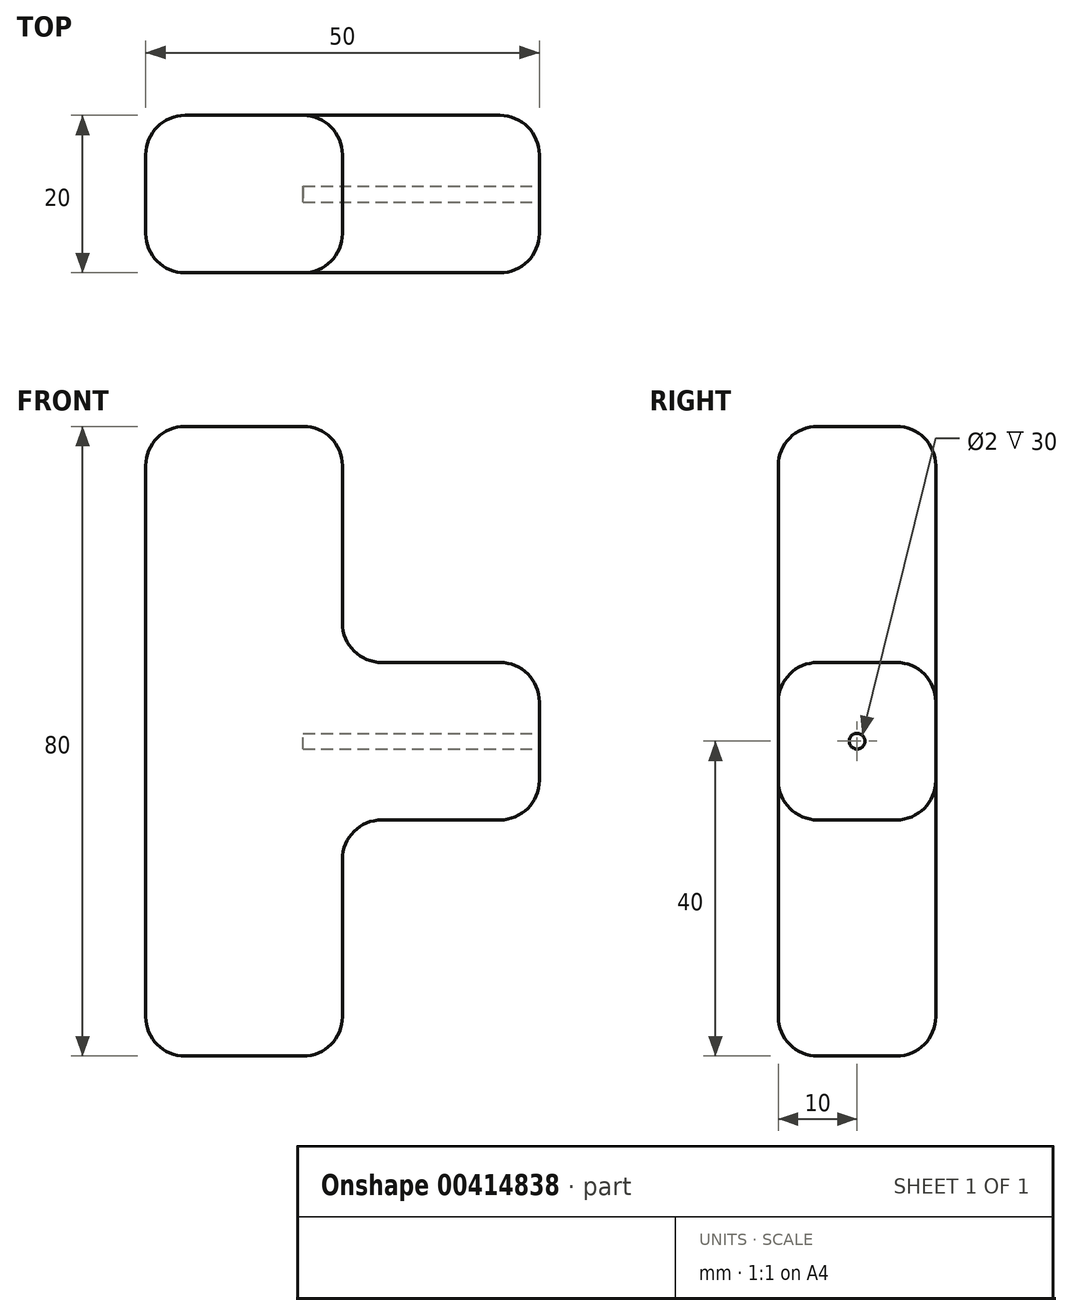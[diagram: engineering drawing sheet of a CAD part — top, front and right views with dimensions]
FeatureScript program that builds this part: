
annotation { "Feature Type Name" : "Feature", "Feature Type Description" : "" }
export const myFeature = defineFeature(function(context is Context, id is Id, definition is map)
    precondition{}
    {
        {
            var Q0;
            Q0=qCreatedBy(makeId("Front.planeOp"),FACE);
            var sketch = newSketch(context, id + "F0", { "sketchPlane" : qUnion([Q0])});
            skLineSegment(sketch, "E0.bottom", {"start": v(0, 0) * mm, "end": v(-25, 0) * mm});
            skLineSegment(sketch, "E0.top", {"start": v(0, 80) * mm, "end": v(-25, 80) * mm});
            skLineSegment(sketch, "E0.left", {"start": v(0, 0) * mm, "end": v(0, 80) * mm});
            skLineSegment(sketch, "E0.right", {"start": v(-25, 0) * mm, "end": v(-25, 80) * mm});
            skLineSegment(sketch, "E1.bottom", {"start": v(0, 30) * mm, "end": v(25, 30) * mm});
            skLineSegment(sketch, "E1.top", {"start": v(0, 50) * mm, "end": v(25, 50) * mm});
            skLineSegment(sketch, "E1.left", {"start": v(0, 30) * mm, "end": v(0, 50) * mm});
            skLineSegment(sketch, "E1.right", {"start": v(25, 30) * mm, "end": v(25, 50) * mm});
            skSolve(sketch);
        }
        {
            var Q0;
            {var subQ3=sQuery(id+"F0.wireOp",EDGE,"E0.bottom");Q0=makeQuery(id+"F0.imprint","IMPRINT",FACE,{"disambiguationData":[TD([[makeQuery(id+"F0.imprint","IMPRINT",EDGE,{"derivedFrom":subQ3}),-1.0]])]});}
            var Q1;
            Q1=makeQuery(id+"F0.imprint","IMPRINT",FACE,{"disambiguationData":[TD([[makeQuery(id+"F0.imprint","IMPRINT",EDGE,{"derivedFrom":sQuery(id+"F0.wireOp",EDGE,"E1.bottom")}),1.0]])]});
            extrude(context, id + "F1", {"entities" : qUnion([Q0, Q1]), "depth" : 20 * mm});
        }
        {
            var Q0;
            {var subQ0=sQuery(id+"F0.wireOp",EDGE,"E0.left");Q0=makeQuery(id+"F1.opExtrude","CAP_EDGE",EDGE,{"disambiguationData":[OSD([subQ0]),TDD([makeQuery(id+"F0.imprint","IMPRINT",EDGE,{"disambiguationData":[TD([[makeQuery(id+"F0.imprint","INTERSECT",VERTEX,{"derivedFrom":[sQuery(id+"F0.wireOp",EDGE,"E0.bottom"),subQ0]}),-1.0]])],"derivedFrom":subQ0})])],"isStart":false});}
            var Q1;
            Q1=makeQuery(id+"F1.opExtrude","SWEPT_EDGE",EDGE,{"disambiguationData":[OSD([sQuery(id+"F0.wireOp",EDGE,"E1.bottom"),sQuery(id+"F0.wireOp",EDGE,"E1.right")])]});
            var Q2;
            Q2=makeQuery(id+"F1.opExtrude","SWEPT_EDGE",EDGE,{"disambiguationData":[OSD([sQuery(id+"F0.wireOp",EDGE,"E0.left"),sQuery(id+"F0.wireOp",EDGE,"E1.bottom"),sQuery(id+"F0.wireOp",EDGE,"E1.left")])]});
            var Q3;
            Q3=makeQuery(id+"F1.opExtrude","SWEPT_EDGE",EDGE,{"disambiguationData":[OSD([sQuery(id+"F0.wireOp",EDGE,"E0.top"),sQuery(id+"F0.wireOp",EDGE,"E0.right")])]});
            var Q4;
            Q4=makeQuery(id+"F1.opExtrude","SWEPT_EDGE",EDGE,{"disambiguationData":[OSD([sQuery(id+"F0.wireOp",EDGE,"E0.top"),sQuery(id+"F0.wireOp",EDGE,"E0.left")])]});
            var Q5;
            Q5=makeQuery(id+"F1.opExtrude","SWEPT_EDGE",EDGE,{"disambiguationData":[OSD([sQuery(id+"F0.wireOp",EDGE,"E0.bottom"),sQuery(id+"F0.wireOp",EDGE,"E0.right")])]});
            var Q6;
            {var subQ0=sQuery(id+"F0.wireOp",EDGE,"E0.left");Q6=makeQuery(id+"F1.opExtrude","CAP_EDGE",EDGE,{"disambiguationData":[OSD([subQ0]),TDD([makeQuery(id+"F0.imprint","IMPRINT",EDGE,{"disambiguationData":[TD([[makeQuery(id+"F0.imprint","INTERSECT",VERTEX,{"derivedFrom":[sQuery(id+"F0.wireOp",EDGE,"E0.top"),subQ0]}),1.0]])],"derivedFrom":subQ0})])],"isStart":false});}
            var Q7;
            {var subQ0=sQuery(id+"F0.wireOp",EDGE,"E0.left");Q7=makeQuery(id+"F1.opExtrude","CAP_EDGE",EDGE,{"disambiguationData":[OSD([subQ0]),TDD([makeQuery(id+"F0.imprint","IMPRINT",EDGE,{"disambiguationData":[TD([[makeQuery(id+"F0.imprint","INTERSECT",VERTEX,{"derivedFrom":[sQuery(id+"F0.wireOp",EDGE,"E0.top"),subQ0]}),1.0]])],"derivedFrom":subQ0})])],"isStart":true});}
            var Q8;
            Q8=makeQuery(id+"F1.opExtrude","SWEPT_EDGE",EDGE,{"disambiguationData":[OSD([sQuery(id+"F0.wireOp",EDGE,"E0.left"),sQuery(id+"F0.wireOp",EDGE,"E1.top"),sQuery(id+"F0.wireOp",EDGE,"E1.left")])]});
            var Q9;
            Q9=makeQuery(id+"F1.opExtrude","SWEPT_EDGE",EDGE,{"disambiguationData":[OSD([sQuery(id+"F0.wireOp",EDGE,"E1.top"),sQuery(id+"F0.wireOp",EDGE,"E1.right")])]});
            var Q10;
            Q10=makeQuery(id+"F1.opExtrude","CAP_EDGE",EDGE,{"disambiguationData":[OSD([sQuery(id+"F0.wireOp",EDGE,"E0.bottom")])],"isStart":true});
            var Q11;
            Q11=makeQuery(id+"F1.opExtrude","CAP_EDGE",EDGE,{"disambiguationData":[OSD([sQuery(id+"F0.wireOp",EDGE,"E0.bottom")])],"isStart":false});
            var Q12;
            Q12=makeQuery(id+"F1.opExtrude","CAP_EDGE",EDGE,{"disambiguationData":[OSD([sQuery(id+"F0.wireOp",EDGE,"E0.top")])],"isStart":true});
            var Q13;
            Q13=makeQuery(id+"F1.opExtrude","CAP_EDGE",EDGE,{"disambiguationData":[OSD([sQuery(id+"F0.wireOp",EDGE,"E0.top")])],"isStart":false});
            var Q14;
            {var subQ0=sQuery(id+"F0.wireOp",EDGE,"E0.left");Q14=makeQuery(id+"F1.opExtrude","CAP_EDGE",EDGE,{"disambiguationData":[OSD([subQ0]),TDD([makeQuery(id+"F0.imprint","IMPRINT",EDGE,{"disambiguationData":[TD([[makeQuery(id+"F0.imprint","INTERSECT",VERTEX,{"derivedFrom":[sQuery(id+"F0.wireOp",EDGE,"E0.bottom"),subQ0]}),-1.0]])],"derivedFrom":subQ0})])],"isStart":true});}
            var Q15;
            Q15=makeQuery(id+"F1.opExtrude","CAP_EDGE",EDGE,{"disambiguationData":[OSD([sQuery(id+"F0.wireOp",EDGE,"E0.right")])],"isStart":true});
            var Q16;
            Q16=makeQuery(id+"F1.opExtrude","CAP_EDGE",EDGE,{"disambiguationData":[OSD([sQuery(id+"F0.wireOp",EDGE,"E0.right")])],"isStart":false});
            var Q17;
            Q17=makeQuery(id+"F1.opExtrude","CAP_EDGE",EDGE,{"disambiguationData":[OSD([sQuery(id+"F0.wireOp",EDGE,"E1.bottom")])],"isStart":true});
            var Q18;
            Q18=makeQuery(id+"F1.opExtrude","CAP_EDGE",EDGE,{"disambiguationData":[OSD([sQuery(id+"F0.wireOp",EDGE,"E1.bottom")])],"isStart":false});
            var Q19;
            Q19=makeQuery(id+"F1.opExtrude","CAP_EDGE",EDGE,{"disambiguationData":[OSD([sQuery(id+"F0.wireOp",EDGE,"E1.top")])],"isStart":true});
            var Q20;
            Q20=makeQuery(id+"F1.opExtrude","CAP_EDGE",EDGE,{"disambiguationData":[OSD([sQuery(id+"F0.wireOp",EDGE,"E1.top")])],"isStart":false});
            var Q21;
            Q21=makeQuery(id+"F1.opExtrude","SWEPT_EDGE",EDGE,{"disambiguationData":[OSD([sQuery(id+"F0.wireOp",EDGE,"E0.bottom"),sQuery(id+"F0.wireOp",EDGE,"E0.left")])]});
            var Q22;
            Q22=makeQuery(id+"F1.opExtrude","CAP_EDGE",EDGE,{"disambiguationData":[OSD([sQuery(id+"F0.wireOp",EDGE,"E1.right")])],"isStart":true});
            var Q23;
            Q23=makeQuery(id+"F1.opExtrude","CAP_EDGE",EDGE,{"disambiguationData":[OSD([sQuery(id+"F0.wireOp",EDGE,"E1.right")])],"isStart":false});
            fillet(context, id + "F2", {"entities" : qUnion([Q0, Q1, Q2, Q3, Q4, Q5, Q6, Q7, Q8, Q9, Q10, Q11, Q12, Q13, Q14, Q15, Q16, Q17, Q18, Q19, Q20, Q21, Q22, Q23]), "radius" : 5 * mm, "tangentPropagation" : true, "allowEdgeOverflow" : false});
        }
        {
            var Q0;
            Q0=makeQuery(id+"F1.opExtrude","SWEPT_FACE",FACE,{"disambiguationData":[OSD([sQuery(id+"F0.wireOp",EDGE,"E1.right")])]});
            var sketch = newSketch(context, id + "F3", { "sketchPlane" : qUnion([Q0])});
            skCircle(sketch, "E2", {"center": v(-10, 40) * mm, "radius": 1 * mm});
            skSolve(sketch);
        }
        {
            var Q0;
            Q0=makeQuery(id+"F3.imprint","IMPRINT",FACE,{"disambiguationData":[TD([[makeQuery(id+"F3.imprint","IMPRINT",EDGE,{"derivedFrom":sQuery(id+"F3.wireOp",EDGE,"E2")}),1.0]])]});
            extrude(context, id + "F4", {"entities" : qUnion([Q0]), "operationType" : NewBodyOperationType.REMOVE, "oppositeDirection" : true, "depth" : 30 * mm});
        }
    });
